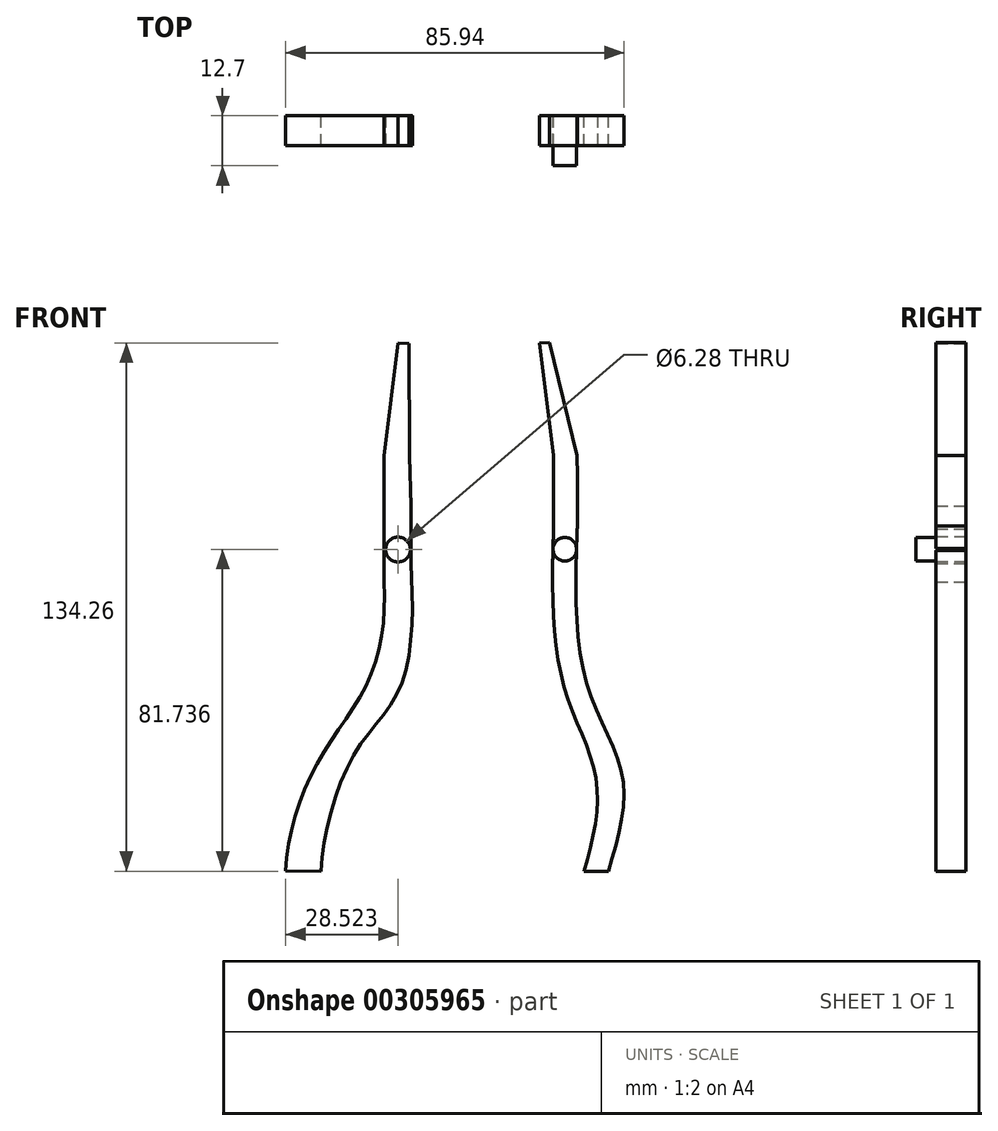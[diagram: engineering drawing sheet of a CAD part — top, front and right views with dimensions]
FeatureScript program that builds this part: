
annotation { "Feature Type Name" : "Feature", "Feature Type Description" : "" }
export const myFeature = defineFeature(function(context is Context, id is Id, definition is map)
    precondition{}
    {
        {
            var Q0;
            Q0=qCreatedBy(makeId("Front.planeOp"),FACE);
            var sketch = newSketch(context, id + "F0", { "sketchPlane" : qUnion([Q0])});
            skFitSpline(sketch, "E0", {"points": [v(39.45, -16.33) * mm, v(42.5, 7.26) * mm, v(34.3, 31.14) * mm, v(31.77, 70.65) * mm], "startDerivative": vector(24.44, 80.27) * mm, "endDerivative": vector(4.1, 109.5) * mm});
            skLineSegment(sketch, "E1", {"start": v(31.24, 56.47) * mm, "end": v(31.5, 56.47) * mm});
            skLineSegment(sketch, "E2", {"start": v(39.45, -16.33) * mm, "end": v(45.64, -16.33) * mm});
            skFitSpline(sketch, "E3", {"points": [v(45.64, -16.33) * mm, v(49.33, 7.26) * mm, v(40.24, 31.14) * mm, v(37.79, 71.4) * mm], "startDerivative": vector(24.4, 80.27) * mm, "endDerivative": vector(4.08, 109.5) * mm});
            skLineSegment(sketch, "E4", {"start": v(37.79, 71.4) * mm, "end": v(37.79, 84.1) * mm});
            skLineSegment(sketch, "E5", {"start": v(31.77, 70.65) * mm, "end": v(31.77, 83.35) * mm});
            skPoint(sketch, "E6.endSnap0", {"position": v(31.77, 77) * mm});
            skPoint(sketch, "E6.end.orphan", {"position": v(31.77, 108.77) * mm});
            skPoint(sketch, "E7.orphan", {"position": v(0, 7.26) * mm});
            skFitSpline(sketch, "E8", {"points": [v(-36.3, -16.3) * mm, v(-28.41, 10.8) * mm, v(-15.24, 32.2) * mm, v(-11.33, 57.11) * mm], "startDerivative": vector(2.7, 76.7) * mm, "endDerivative": vector(-4.97, 79.8) * mm});
            skPoint(sketch, "E9.orphan", {"position": v(0, 31.14) * mm});
            skFitSpline(sketch, "E10", {"points": [v(-27.29, -16.33) * mm, v(-18.8, 13.54) * mm, v(-6.92, 31.14) * mm, v(-4.48, 61.8) * mm], "startDerivative": vector(2.7, 76.7) * mm, "endDerivative": vector(-4.97, 79.8) * mm});
            skLineSegment(sketch, "E11", {"start": v(-36.3, -16.3) * mm, "end": v(-27.29, -16.33) * mm});
            skLineSegment(sketch, "E12", {"start": v(-4.48, 61.8) * mm, "end": v(-4.47, 76.4) * mm});
            skLineSegment(sketch, "E13", {"start": v(-4.84, 89.1) * mm, "end": v(-4.47, 76.4) * mm});
            skLineSegment(sketch, "E14", {"start": v(-11.33, 57.11) * mm, "end": v(-11.32, 70.65) * mm});
            skLineSegment(sketch, "E15", {"start": v(-11.32, 70.65) * mm, "end": v(-11.33, 79.6) * mm});
            skPoint(sketch, "E16.orphan", {"position": v(-5.01, 103.15) * mm});
            skPoint(sketch, "E17.end.orphan", {"position": v(4.54, 103.15) * mm});
            skPoint(sketch, "E18.end.orphan", {"position": v(-0.24, 103.15) * mm});
            skPoint(sketch, "E19.start.orphan", {"position": v(28.94, 108.77) * mm});
            skLineSegment(sketch, "E20", {"start": v(-11.33, 79.6) * mm, "end": v(-11.33, 85.98) * mm});
            skLineSegment(sketch, "E21", {"start": v(-11.33, 85.98) * mm, "end": v(-11.33, 89.1) * mm});
            skLineSegment(sketch, "E22", {"start": v(-11.33, 89.1) * mm, "end": v(-7.77, 117.88) * mm});
            skPoint(sketch, "E23.end.orphan", {"position": v(-5.01, 113.48) * mm});
            skLineSegment(sketch, "E24", {"start": v(-4.84, 89.1) * mm, "end": v(-5.01, 117.73) * mm});
            skLineSegment(sketch, "E25", {"start": v(-5.01, 117.73) * mm, "end": v(-7.77, 117.88) * mm});
            skPoint(sketch, "E26.start.orphan", {"position": v(0, 112.99) * mm});
            skLineSegment(sketch, "E27", {"start": v(28.15, 117.92) * mm, "end": v(30.77, 117.93) * mm});
            skLineSegment(sketch, "E28", {"start": v(31.77, 83.35) * mm, "end": v(31.77, 89.32) * mm});
            skLineSegment(sketch, "E29", {"start": v(37.79, 84.1) * mm, "end": v(37.76, 89.35) * mm});
            skLineSegment(sketch, "E30", {"start": v(31.77, 89.32) * mm, "end": v(28.15, 117.92) * mm});
            skLineSegment(sketch, "E31", {"start": v(37.76, 89.35) * mm, "end": v(30.77, 117.93) * mm});
            skSolve(sketch);
        }
        {
            var Q0;
            {var subQ0=sQuery(id+"F0.wireOp",EDGE,"E2");Q0=makeQuery(id+"F0.imprint","IMPRINT",FACE,{"disambiguationData":[TD([[makeQuery(id+"F0.imprint","IMPRINT",EDGE,{"derivedFrom":subQ0}),1.0]])]});}
            extrude(context, id + "F1", {"entities" : qUnion([Q0]), "depth" : 7.62 * mm});
        }
        {
            var Q0;
            Q0=makeQuery(id+"F0.imprint","IMPRINT",FACE,{"disambiguationData":[TD([[makeQuery(id+"F0.imprint","IMPRINT",EDGE,{"derivedFrom":sQuery(id+"F0.wireOp",EDGE,"E8")}),-1.0]])]});
            extrude(context, id + "F2", {"entities" : qUnion([Q0]), "depth" : 7.62 * mm});
        }
        {
            var Q0;
            Q0=qCreatedBy(makeId("Front.planeOp"),FACE);
            var sketch = newSketch(context, id + "F3", { "sketchPlane" : qUnion([Q0])});
            skCircle(sketch, "E32", {"center": v(34.6, 65.47) * mm, "radius": 3 * mm});
            skCircle(sketch, "E33", {"center": v(-7.56, 65.47) * mm, "radius": 3.73 * mm});
            skSolve(sketch);
        }
        {
            var Q0;
            Q0=sQuery(id+"F3.wireOp",EDGE,"E33");
            extrude(context, id + "F4", {"bodyType" : ToolBodyType.SURFACE, "operationType" : NewBodyOperationType.REMOVE, "surfaceEntities" : qUnion([Q0]), "oppositeDirection" : true, "depth" : 7.62 * mm});
        }
        {
            var Q0;
            Q0=makeQuery(id+"F3.imprint","IMPRINT",FACE,{"disambiguationData":[TD([[makeQuery(id+"F3.imprint","IMPRINT",EDGE,{"derivedFrom":sQuery(id+"F3.wireOp",EDGE,"E32")}),1.0]])]});
            var Q1;
            Q1=sQuery(id+"F3.wireOp",EDGE,"E32");
            extrude(context, id + "F5", {"entities" : qUnion([Q0]), "operationType" : NewBodyOperationType.ADD, "surfaceEntities" : qUnion([Q1]), "depth" : 12.7 * mm});
        }
        {
            var Q0;
            Q0=makeQuery(id+"F3.imprint","IMPRINT",FACE,{"disambiguationData":[TD([[makeQuery(id+"F3.imprint","IMPRINT",EDGE,{"derivedFrom":sQuery(id+"F3.wireOp",EDGE,"E33")}),1.0]])]});
            extrude(context, id + "F6", {"entities" : qUnion([Q0]), "operationType" : NewBodyOperationType.REMOVE, "oppositeDirection" : true, "depth" : 25.4 * mm});
        }
        {
            var Q0;
            Q0=makeQuery(id+"F2.opExtrude","CAP_FACE",FACE,{"disambiguationData":[OSD([sQuery(id+"F0.wireOp",EDGE,"E8"),sQuery(id+"F0.wireOp",EDGE,"E10"),sQuery(id+"F0.wireOp",EDGE,"E11"),sQuery(id+"F0.wireOp",EDGE,"E12"),sQuery(id+"F0.wireOp",EDGE,"E13"),sQuery(id+"F0.wireOp",EDGE,"E14"),sQuery(id+"F0.wireOp",EDGE,"E15"),sQuery(id+"F0.wireOp",EDGE,"E20"),sQuery(id+"F0.wireOp",EDGE,"E21"),sQuery(id+"F0.wireOp",EDGE,"E22"),sQuery(id+"F0.wireOp",EDGE,"E24"),sQuery(id+"F0.wireOp",EDGE,"E25")])],"isStart":false});
            var sketch = newSketch(context, id + "F7", { "sketchPlane" : qUnion([Q0])});
            skLineSegment(sketch, "E34", {"start": v(-7.68, 68.54) * mm, "end": v(-7.77, 65.4) * mm});
            skCircle(sketch, "E35", {"center": v(-7.77, 65.4) * mm, "radius": 3.14 * mm});
            skPoint(sketch, "E36.orphan", {"position": v(-6.39, 117.8) * mm});
            skSolve(sketch);
        }
        {
            var Q0;
            Q0=makeQuery(id+"F7.imprint","IMPRINT",FACE,{"disambiguationData":[TD([[makeQuery(id+"F7.imprint","IMPRINT",EDGE,{"derivedFrom":sQuery(id+"F7.wireOp",EDGE,"E35")}),1.0]])]});
            extrude(context, id + "F8", {"entities" : qUnion([Q0]), "operationType" : NewBodyOperationType.REMOVE, "oppositeDirection" : true, "depth" : 25.4 * mm});
        }
    });
